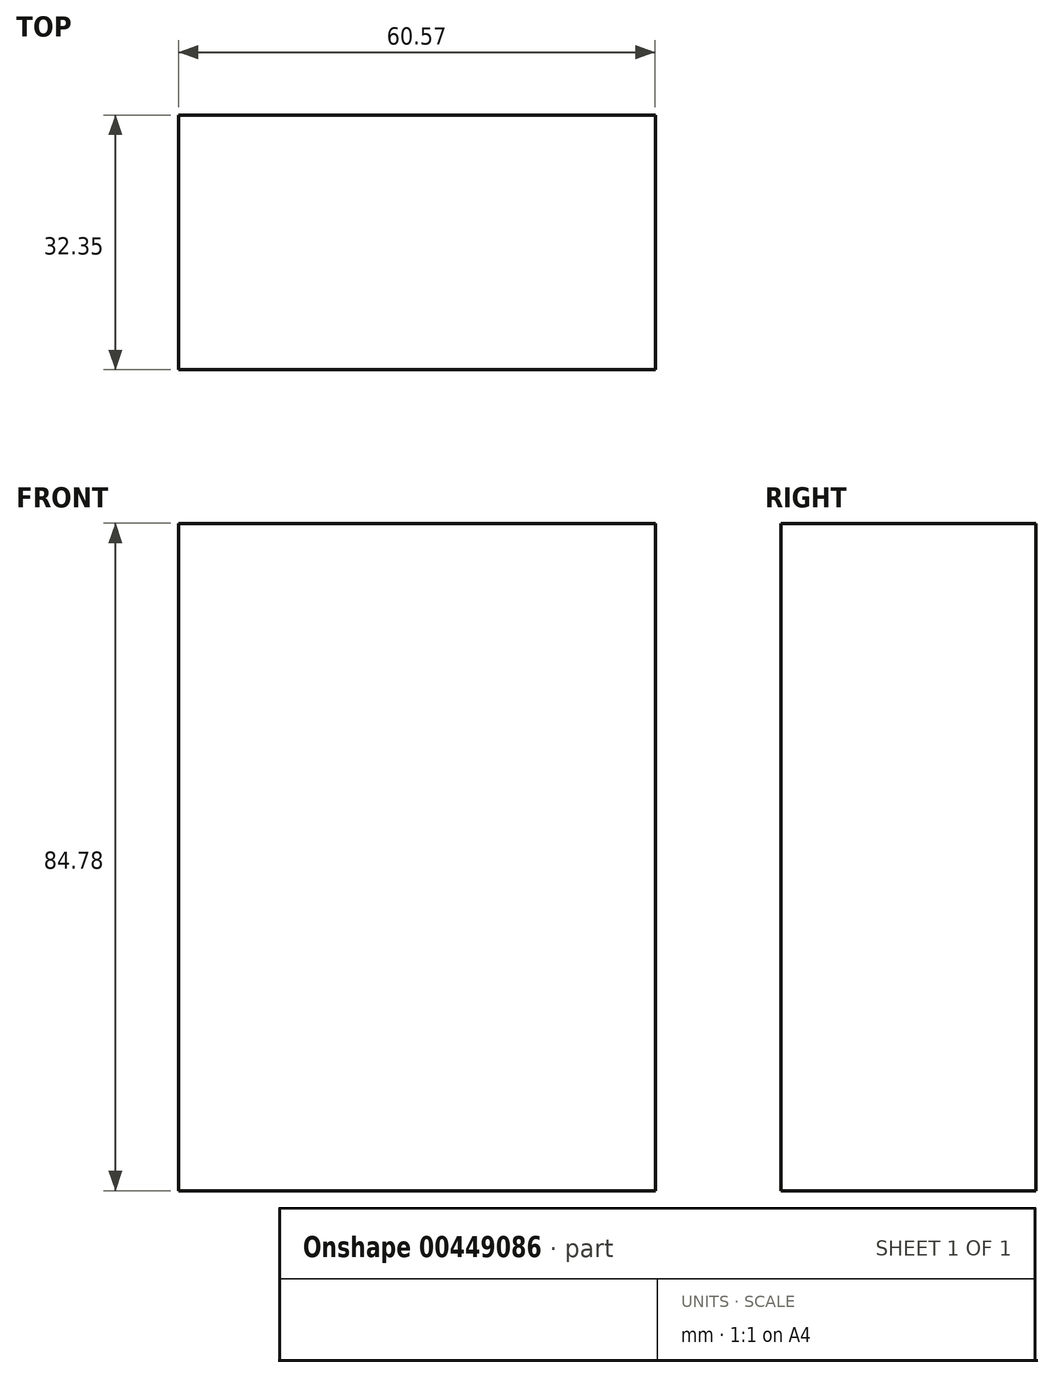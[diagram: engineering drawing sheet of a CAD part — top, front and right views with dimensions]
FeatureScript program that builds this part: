
annotation { "Feature Type Name" : "Feature", "Feature Type Description" : "" }
export const myFeature = defineFeature(function(context is Context, id is Id, definition is map)
    precondition{}
    {
        {
            var Q0;
            Q0=qCreatedBy(makeId("Front.planeOp"),FACE);
            var sketch = newSketch(context, id + "F0", { "sketchPlane" : qUnion([Q0])});
            skLineSegment(sketch, "E0.bottom", {"start": v(38.1, 18.77) * mm, "end": v(-22.47, 18.77) * mm});
            skLineSegment(sketch, "E0.top", {"start": v(38.1, -20.61) * mm, "end": v(-22.47, -20.61) * mm});
            skLineSegment(sketch, "E0.left", {"start": v(38.1, 18.77) * mm, "end": v(38.1, -20.61) * mm});
            skLineSegment(sketch, "E0.right", {"start": v(-22.47, 18.77) * mm, "end": v(-22.47, -20.61) * mm});
            skSolve(sketch);
        }
        {
            var Q0;
            Q0=makeQuery(id+"F0.imprint","IMPRINT",FACE,{"disambiguationData":[TD([[makeQuery(id+"F0.imprint","IMPRINT",EDGE,{"derivedFrom":sQuery(id+"F0.wireOp",EDGE,"E0.bottom")}),1.0]])]});
            extrude(context, id + "F1", {"entities" : qUnion([Q0]), "depth" : 32.35 * mm});
        }
        {
            var Q0;
            Q0=makeQuery(id+"F1.opExtrude","SWEPT_FACE",FACE,{"disambiguationData":[OSD([sQuery(id+"F0.wireOp",EDGE,"E0.bottom")])]});
            extrude(context, id + "F2", {"entities" : qUnion([Q0]), "operationType" : NewBodyOperationType.ADD, "depth" : 45.4 * mm});
        }
    });
